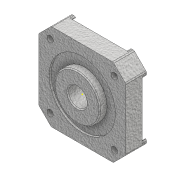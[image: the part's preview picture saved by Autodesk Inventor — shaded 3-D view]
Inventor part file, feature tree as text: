
AUTODESK INVENTOR PART (.ipt)
format: ipt  version: 2018 (Build 220112000, 112)  size: 238,080 bytes
history: native  units: mm
features: sketch x8, extrude x6, mirror x4, fillet x4, projected_geometry x2, chamfer x1
ambient origin geometry x8: Origin, YZ Plane, XZ Plane, XY Plane, X Axis, Y Axis, Z Axis, Center Point
bodies: Solid1 (feature_tree)
feature tree (25):
  extrude  "Extrusion1"  Depth=42.0mm
  sketch  "Sketch2"  dims[d4=6.0mm d5=2.0mm d6=45.0deg d7=2.0mm d8=0.0mm d10=1.0mm d11=1.0mm]
  chamfer  "Chamfer1"  Distance=8.0mm
  extrude  "Extrusion2"  Depth=2.0mm TaperAngle=0.0deg
  mirror  "Mirror1"
  mirror  "Mirror2"
  fillet  "Fillet2"  Radius=1.0mm
  fillet  "Fillet3"  Radius=1.0mm
  extrude  "Extrusion3"  Depth=1.0mm
  extrude  "Extrusion4"  Depth=22.0mm
  extrude  "Extrusion5"  Depth=2.5mm TaperAngle=0.0deg
  sketch  "Sketch7"  dims[d25=5.5mm]
  extrude  "Extrusion6"  Depth=2.5mm TaperAngle=0.0deg
  mirror  "Mirror3"
  mirror  "Mirror4"
  fillet  "Fillet4"  Radius=3.0mm
  fillet  "Fillet5"  Radius=5.5mm
  sketch  "Sketch1"  dims[d0=42.0mm d1=42.0mm d2=8.0mm d3=0.0mm]
  sketch  "Sketch3"  dims[d12=1.0mm d13=1.0mm]
  projected_geometry  "Projected Loop1"
  sketch  "Sketch4"  dims[d14=32.0mm d15=22.0mm]
  sketch  "Sketch5"  dims[d16=1.0mm d17=0.0mm d18=2.5mm d19=0.0mm]
  projected_geometry  "Projected Loop2"
  sketch  "Sketch6"  dims[d20=9.0mm d21=2.5mm d22=0.0mm d23=3.0mm d24=5.5mm]
  sketch  "Sketch8"  dims[d26=5.0mm d27=0.0mm d28=0.5mm d29=0.5mm]
